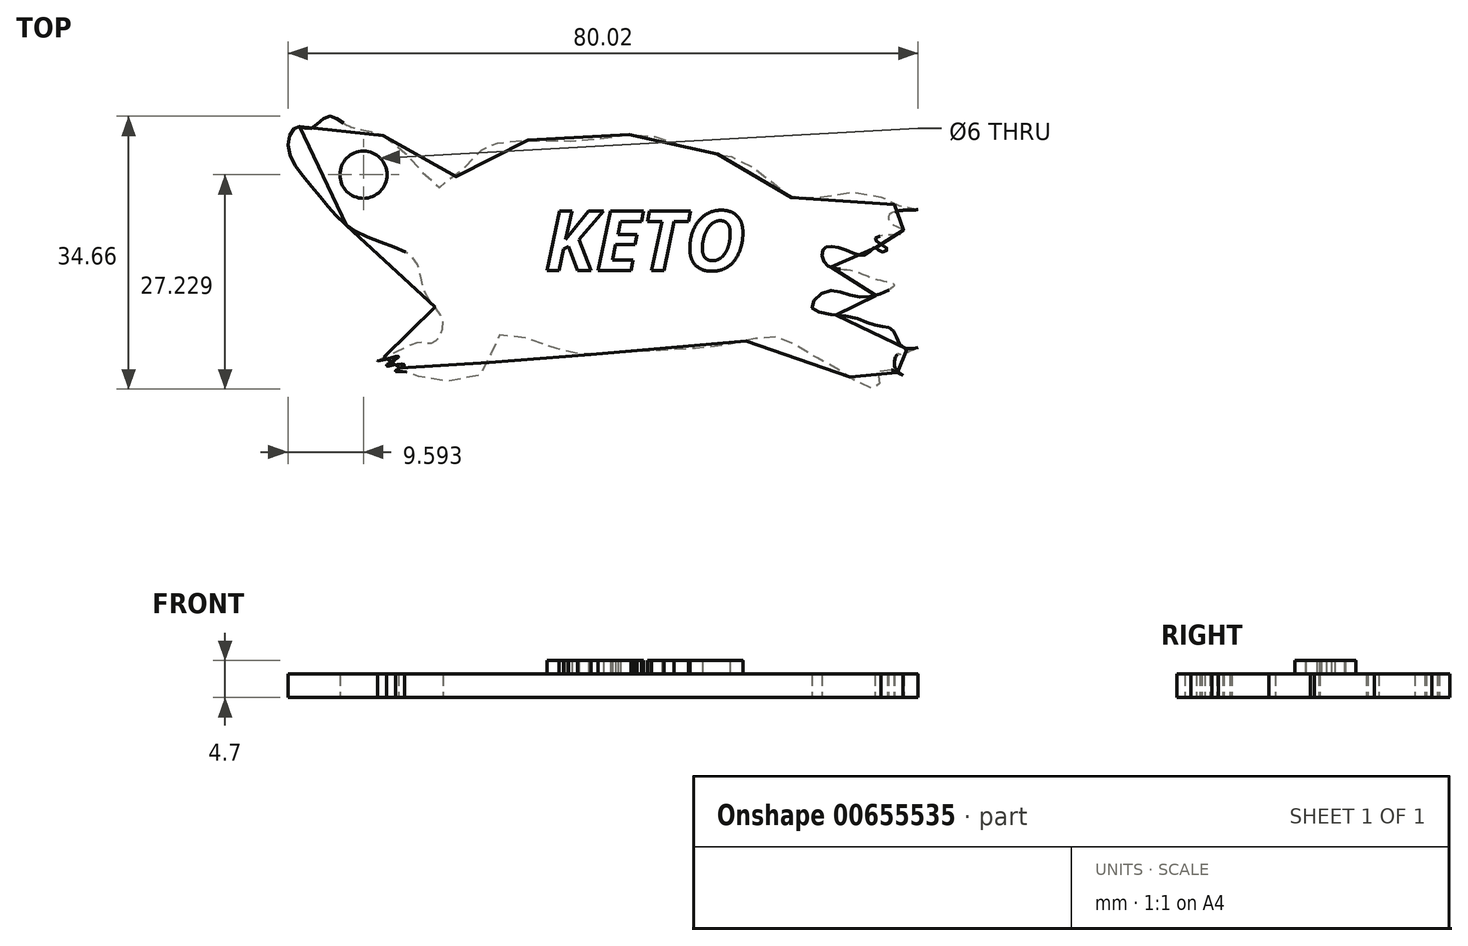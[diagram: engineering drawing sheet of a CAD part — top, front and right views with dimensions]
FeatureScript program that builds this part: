
annotation { "Feature Type Name" : "Feature", "Feature Type Description" : "" }
export const myFeature = defineFeature(function(context is Context, id is Id, definition is map)
    precondition{}
    {
        {
            var Q0;
            Q0=qCreatedBy(makeId("Top.planeOp"),FACE);
            var sketch = newSketch(context, id + "F0", { "sketchPlane" : qUnion([Q0])});
            skFitSpline(sketch, "E0", {"points": [v(-67.91, 32) * mm, v(-64.82, 29.46) * mm, v(-63, 27.36) * mm, v(-60.89, 25.4) * mm, v(-56.82, 28.76) * mm, v(-55.41, 30.17) * mm, v(-54.29, 30.87) * mm, v(-51.9, 31.15) * mm, v(-48.95, 31.43) * mm, v(-46.7, 31.3) * mm, v(-42.21, 31.43) * mm, v(-37.3, 32) * mm, v(-34.9, 32.13) * mm, v(-31.26, 31.15) * mm, v(-28.3, 30.17) * mm, v(-25.36, 29.6) * mm, v(-21.85, 28.62) * mm, v(-20.16, 27.22) * mm, v(-17.78, 25.53) * mm, v(-15.8, 23.99) * mm, v(-11.17, 24.4) * mm, v(-5.42, 24.55) * mm, v(-3.31, 23.29) * mm, v(-1.34, 23) * mm, v(0, 22.58) * mm, v(-3.31, 22.16) * mm, v(-3.45, 20.9) * mm, v(-1.77, 19.92) * mm, v(-2.05, 19.5) * mm, v(-3.6, 19.35) * mm, v(-5.42, 18.8) * mm, v(-3.87, 17.53) * mm, v(-4.71, 17.25) * mm, v(-5.42, 17.8) * mm, v(-6.68, 16.83) * mm, v(-9.77, 17.67) * mm, v(-12.02, 17.53) * mm, v(-11.6, 15.56) * mm, v(-8.5, 14.86) * mm, v(-5.28, 13.74) * mm, v(-3.03, 13.03) * mm, v(-4.57, 11.91) * mm, v(-8.23, 11.63) * mm, v(-11.6, 12.2) * mm, v(-13.42, 10.08) * mm, v(-8.65, 8.96) * mm, v(-5.28, 7.84) * mm, v(-3.6, 7.56) * mm, v(-2.75, 6.43) * mm, v(-1.63, 4.89) * mm, v(0, 5.03) * mm, v(-2.19, 4.19) * mm, v(-2.6, 4.19) * mm, v(-2.89, 2.5) * mm, v(-1.9, 1.52) * mm, v(-3.03, 2.08) * mm, v(-3.6, 2.22) * mm, v(-5.42, 1.66) * mm, v(-4.71, 0) * mm, v(-6.4, 0) * mm, v(-9.35, 1.8) * mm, v(-14.12, 4.47) * mm, v(-18.06, 6.43) * mm, v(-23.81, 5.45) * mm, v(-34.49, 4.6) * mm, v(-41.79, 4.19) * mm, v(-46.28, 5.03) * mm, v(-53.45, 6.43) * mm, v(-55.27, 1.8) * mm, v(-63.56, 1.38) * mm, v(-64.82, 1.94) * mm, v(-66.37, 2.08) * mm, v(-65.24, 2.78) * mm, v(-65.94, 2.92) * mm, v(-67.49, 2.78) * mm, v(-65.94, 3.9) * mm, v(-68.61, 3.34) * mm, v(-65.8, 4.75) * mm, v(-63, 5.73) * mm, v(-61.45, 5.73) * mm, v(-60.33, 8.4) * mm, v(-62.57, 11.91) * mm, v(-63.98, 16.26) * mm, v(-71.14, 19.63) * mm, v(-76.34, 24.7) * mm, v(-80, 30.59) * mm, v(-78.72, 33.12) * mm, v(-77.18, 32.84) * mm, v(-74.93, 34.4) * mm, v(-72.4, 33.26) * mm, v(-67.91, 32) * mm]});
            skSolve(sketch);
        }
        {
            var Q0;
            Q0=qCreatedBy(makeId("Top.planeOp"),FACE);
            var sketch = newSketch(context, id + "F1", { "sketchPlane" : qUnion([Q0])});
            skText(sketch, "E1", { "text": "KETO", "fontName": "OpenSans-BoldItalic.ttf"});
            const initialGuessF1  = {"E1": [-0.0474, 0.01484, 1, 0, 0.0076]};
            skSetInitialGuess(sketch, initialGuessF1);
            skSolve(sketch);
        }
        {
            var Q0;
            Q0=qCreatedBy(makeId("Top.planeOp"),FACE);
            var sketch = newSketch(context, id + "F2", { "sketchPlane" : qUnion([Q0])});
            skCircle(sketch, "E2", {"center": v(-70.42, 27) * mm, "radius": 4 * mm});
            skSolve(sketch);
        }
        {
            var Q0;
            Q0=makeQuery(id+"F0.imprint","IMPRINT",FACE,{"disambiguationData":[TD([[makeQuery(id+"F0.imprint","IMPRINT",EDGE,{"derivedFrom":sQuery(id+"F0.wireOp",EDGE,"E0")}),-1.0]])]});
            extrude(context, id + "F3", {"entities" : qUnion([Q0]), "depth" : 3 * mm, "offsetDistance" : 25 * mm});
        }
        {
            var Q0;
            Q0 = qSketchRegion(id + "F1", true);
            extrude(context, id + "F4", {"entities" : qUnion([Q0]), "operationType" : NewBodyOperationType.ADD, "depth" : 4.7 * mm, "offsetDistance" : 25 * mm});
        }
        {
            var Q0;
            Q0=sQuery(id+"F2.wireOp",VERTEX,"E2.center");
            var Q1;
            Q1=makeQuery(id+"F3.opExtrude","SWEPT_BODY",BODY,{"disambiguationData":[OSD([sQuery(id+"F0.wireOp",EDGE,"E0")])]});
            hole(context, id + "F5", {"style" : HoleStyle.SIMPLE, "endStyle" : HoleEndStyle.THROUGH, "oppositeDirection" : true, "holeDiameter" : 6 * mm, "majorDiameter" : 5 * mm, "isTappedThrough" : true, "tappedDepth" : 12 * mm, "tapClearance" : 3, "locations" : qUnion([Q0]), "scope" : qUnion([Q1])});
        }
    });
